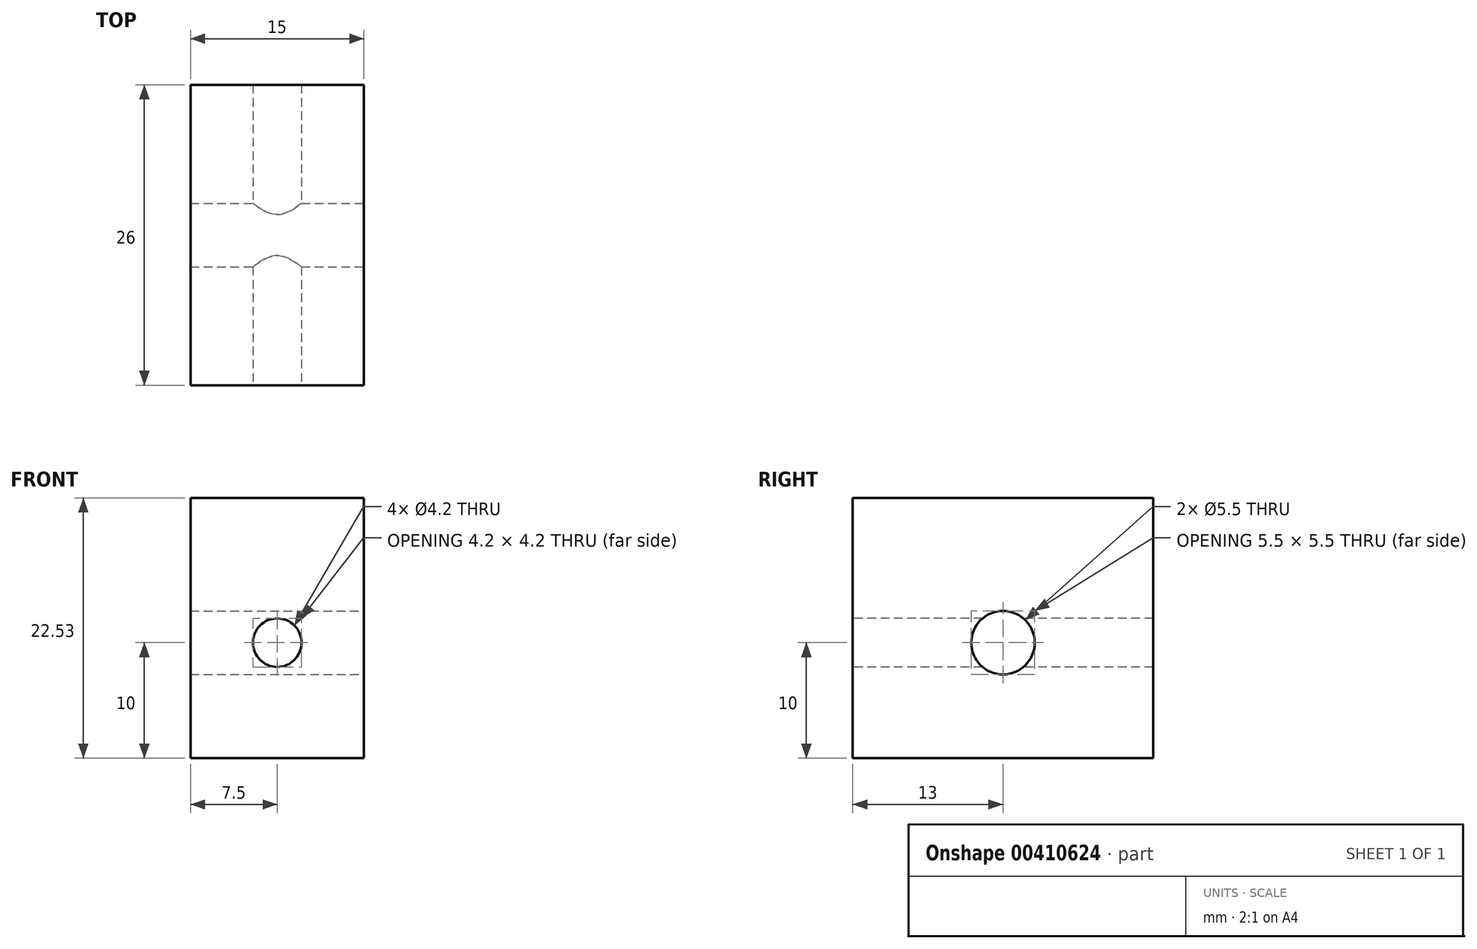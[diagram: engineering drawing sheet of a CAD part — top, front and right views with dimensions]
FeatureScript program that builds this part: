
annotation { "Feature Type Name" : "Feature", "Feature Type Description" : "" }
export const myFeature = defineFeature(function(context is Context, id is Id, definition is map)
    precondition{}
    {
        {
            var Q0;
            Q0=qCreatedBy(makeId("Top.planeOp"),FACE);
            var sketch = newSketch(context, id + "F0", { "sketchPlane" : qUnion([Q0])});
            skLineSegment(sketch, "E0.bottom", {"start": v(0, 0) * mm, "end": v(15, 0) * mm});
            skLineSegment(sketch, "E0.top", {"start": v(0, 26) * mm, "end": v(15, 26) * mm});
            skLineSegment(sketch, "E0.left", {"start": v(0, 0) * mm, "end": v(0, 26) * mm});
            skLineSegment(sketch, "E0.right", {"start": v(15, 0) * mm, "end": v(15, 26) * mm});
            skSolve(sketch);
        }
        {
            var Q0;
            Q0 = qSketchRegion(id + "F0", true);
            extrude(context, id + "F1", {"entities" : qUnion([Q0]), "depth" : 22.53 * mm});
        }
        {
            var Q0;
            Q0=makeQuery(id+"F1.opExtrude","SWEPT_FACE",FACE,{"disambiguationData":[OSD([sQuery(id+"F0.wireOp",EDGE,"E0.bottom")])]});
            var sketch = newSketch(context, id + "F2", { "sketchPlane" : qUnion([Q0])});
            skPoint(sketch, "E1", {"position": v(7.5, 10) * mm});
            skSolve(sketch);
        }
        {
            var Q0;
            Q0=sQuery(id+"F2.wireOp",VERTEX,"E1");
            var Q1;
            Q1=makeQuery(id+"F1.opExtrude","SWEPT_BODY",BODY,{"disambiguationData":[OSD([sQuery(id+"F0.wireOp",EDGE,"E0.bottom"),sQuery(id+"F0.wireOp",EDGE,"E0.top"),sQuery(id+"F0.wireOp",EDGE,"E0.left"),sQuery(id+"F0.wireOp",EDGE,"E0.right")])]});
            hole(context, id + "F3", {"style" : HoleStyle.SIMPLE, "endStyle" : HoleEndStyle.THROUGH, "standardTappedOrClearance" : lookupTablePath({ "standard" : "ISO", "engagement" : "75%", "pitch" : "0.8 mm", "size" : "M5", "type" : "Tapped" }), "standardBlindInLast" : lookupTablePath({ "standard" : "ISO", "engagement" : "75%", "pitch" : "0.8 mm", "size" : "M5", "type" : "Tapped" }), "holeDiameter" : 4.2 * mm, "showTappedDepth" : true, "isTappedThrough" : true, "tappedDepth" : 2.6 * mm, "tapClearance" : 3, "locations" : qUnion([Q0]), "scope" : qUnion([Q1]), "majorDiameter" : 5 * mm});
        }
        {
            var Q0;
            Q0=makeQuery(id+"F1.opExtrude","SWEPT_FACE",FACE,{"disambiguationData":[OSD([sQuery(id+"F0.wireOp",EDGE,"E0.right")])]});
            var sketch = newSketch(context, id + "F4", { "sketchPlane" : qUnion([Q0])});
            skPoint(sketch, "E2", {"position": v(13, 10) * mm});
            skSolve(sketch);
        }
        {
            var Q0;
            Q0=sQuery(id+"F4.wireOp",VERTEX,"E2");
            var Q1;
            Q1=makeQuery(id+"F1.opExtrude","SWEPT_BODY",BODY,{"disambiguationData":[OSD([sQuery(id+"F0.wireOp",EDGE,"E0.bottom"),sQuery(id+"F0.wireOp",EDGE,"E0.top"),sQuery(id+"F0.wireOp",EDGE,"E0.left"),sQuery(id+"F0.wireOp",EDGE,"E0.right")])]});
            hole(context, id + "F5", {"style" : HoleStyle.SIMPLE, "endStyle" : HoleEndStyle.THROUGH, "standardTappedOrClearance" : lookupTablePath({ "standard" : "ISO", "size" : "5.5", "type" : "Drilled" }), "standardBlindInLast" : lookupTablePath({ "standard" : "ISO", "size" : "5.5", "type" : "Drilled" }), "holeDiameter" : 5.5 * mm, "isTappedThrough" : true, "tappedDepth" : 2.6 * mm, "tapClearance" : 3, "locations" : qUnion([Q0]), "scope" : qUnion([Q1])});
        }
    });
